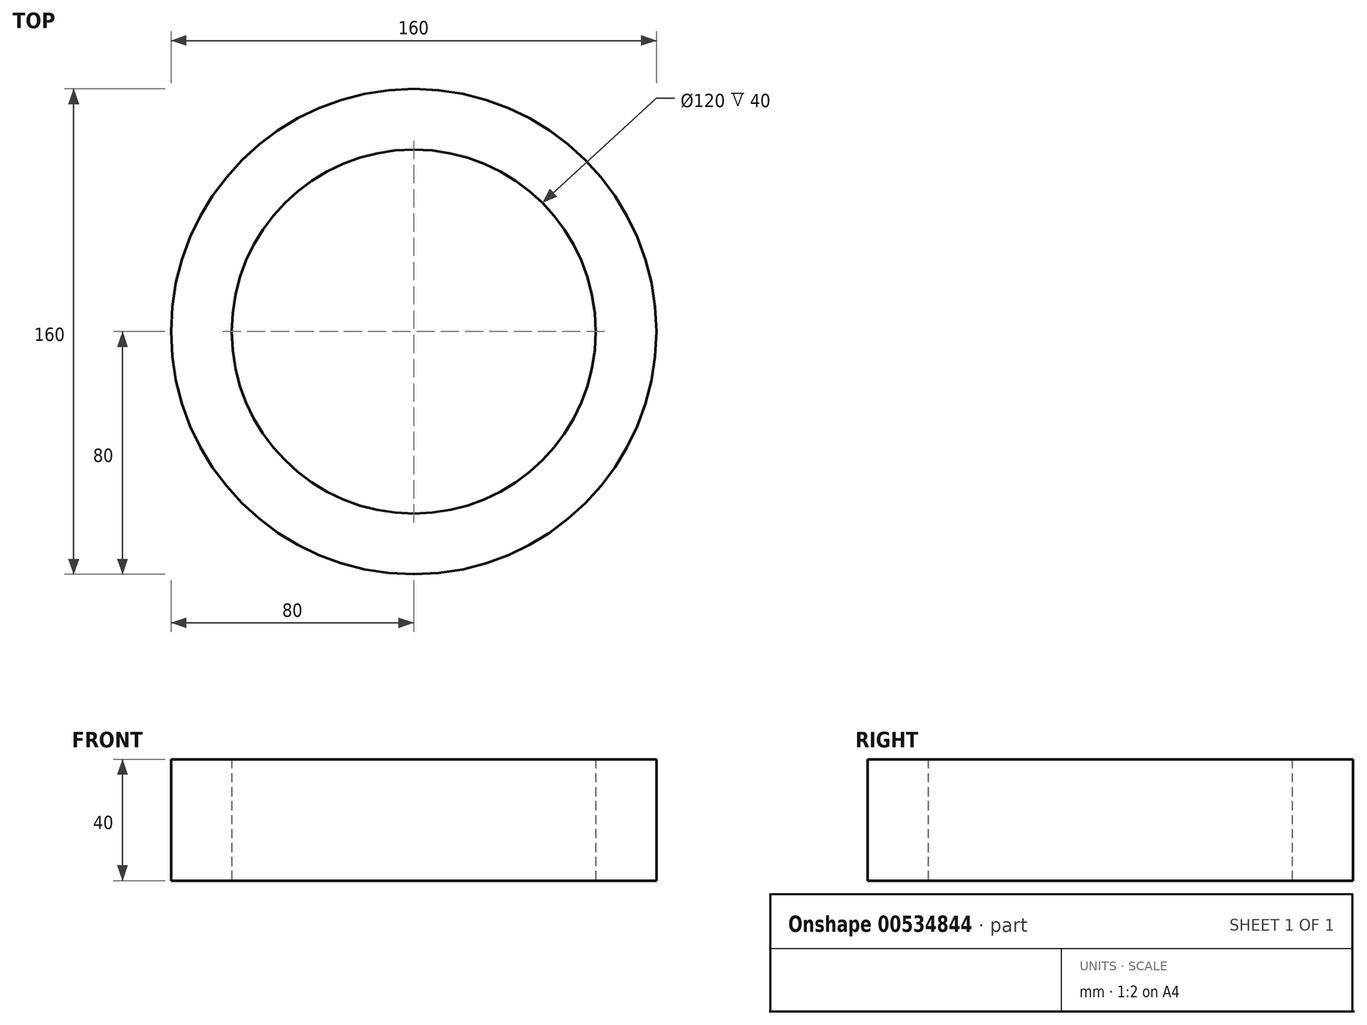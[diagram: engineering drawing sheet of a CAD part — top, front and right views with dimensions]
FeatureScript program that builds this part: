
annotation { "Feature Type Name" : "Feature", "Feature Type Description" : "" }
export const myFeature = defineFeature(function(context is Context, id is Id, definition is map)
    precondition{}
    {
        {
            var Q0;
            Q0=qCreatedBy(makeId("Top.planeOp"),FACE);
            var sketch = newSketch(context, id + "F0", { "sketchPlane" : qUnion([Q0])});
            skCircle(sketch, "E0", {"center": v(0, 0) * mm, "radius": 80 * mm});
            skSolve(sketch);
        }
        {
            var Q0;
            Q0=makeQuery(id+"F0.imprint","IMPRINT",FACE,{"disambiguationData":[TD([[makeQuery(id+"F0.imprint","IMPRINT",EDGE,{"derivedFrom":sQuery(id+"F0.wireOp",EDGE,"E0")}),1.0]])]});
            extrude(context, id + "F1", {"entities" : qUnion([Q0]), "depth" : 40 * mm, "offsetDistance" : 25 * mm});
        }
        {
            var Q0;
            Q0=makeQuery(id+"F0.imprint","IMPRINT",FACE,{"disambiguationData":[TD([[makeQuery(id+"F0.imprint","IMPRINT",EDGE,{"derivedFrom":sQuery(id+"F0.wireOp",EDGE,"E0")}),1.0]])]});
            var sketch = newSketch(context, id + "F2", { "sketchPlane" : qUnion([Q0])});
            skCircle(sketch, "E1", {"center": v(0, 0) * mm, "radius": 60 * mm});
            skSolve(sketch);
        }
        {
            var Q0;
            Q0 = qSketchRegion(id + "F2", true);
            extrude(context, id + "F3", {"entities" : qUnion([Q0]), "operationType" : NewBodyOperationType.REMOVE, "endBound" : BoundingType.THROUGH_ALL, "depth" : 25 * mm, "offsetDistance" : 25 * mm});
        }
    });
